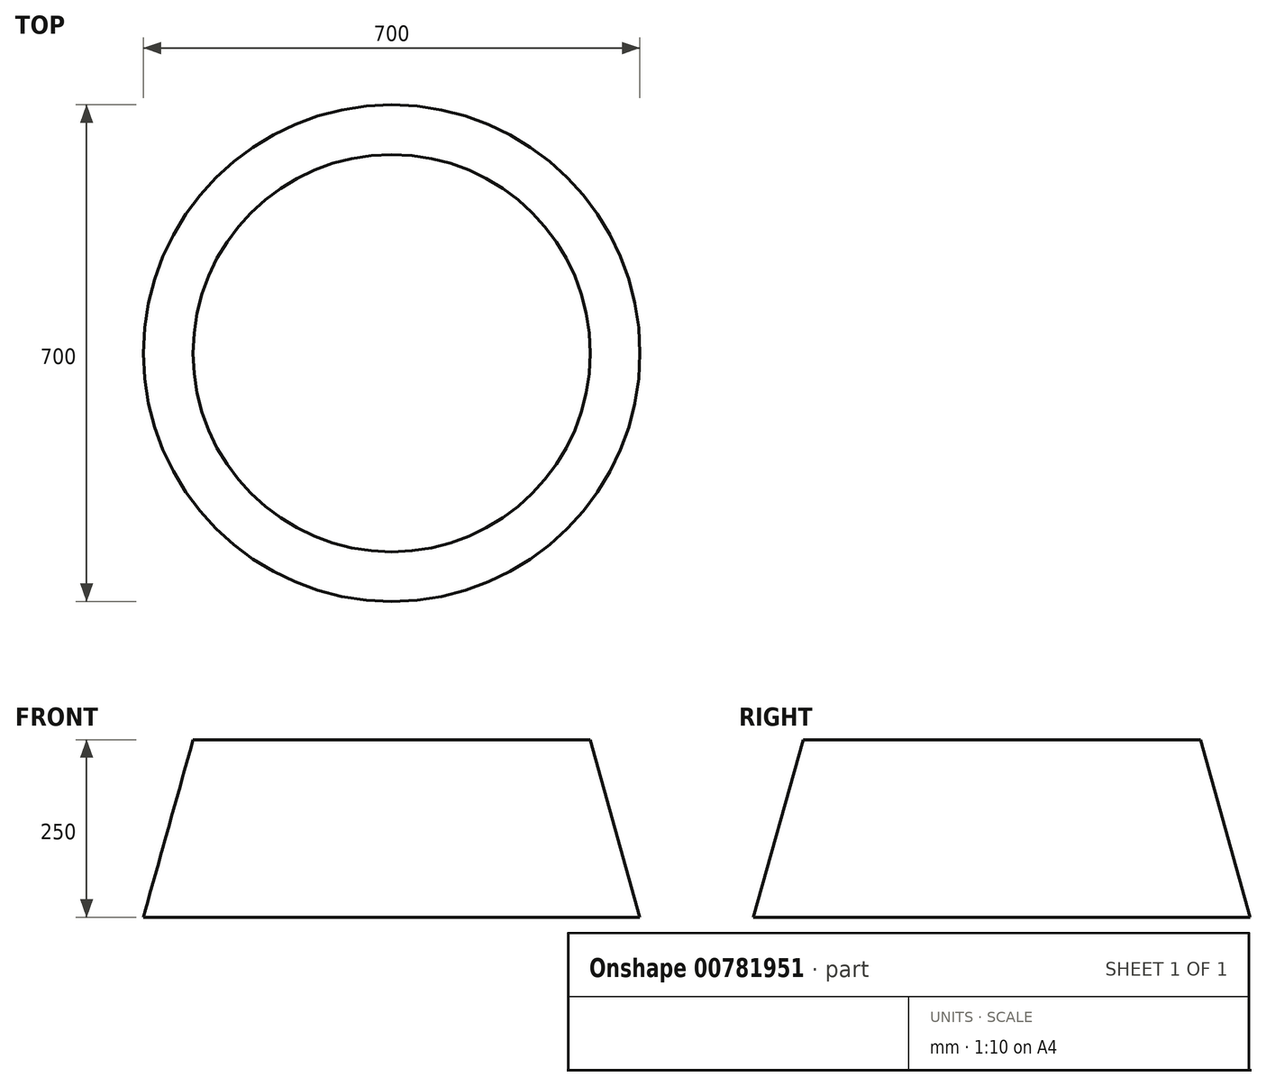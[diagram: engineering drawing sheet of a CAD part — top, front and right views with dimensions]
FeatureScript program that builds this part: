
annotation { "Feature Type Name" : "Feature", "Feature Type Description" : "" }
export const myFeature = defineFeature(function(context is Context, id is Id, definition is map)
    precondition{}
    {
        {
            var Q0;
            Q0=qCreatedBy(makeId("Front.planeOp"),FACE);
            var sketch = newSketch(context, id + "F0", { "sketchPlane" : qUnion([Q0])});
            skLineSegment(sketch, "E0", {"start": v(350, 0) * mm, "end": v(0, 0) * mm});
            skLineSegment(sketch, "E1", {"start": v(0, 0) * mm, "end": v(0, 250) * mm});
            skLineSegment(sketch, "E2", {"start": v(0, 250) * mm, "end": v(280, 250) * mm});
            skLineSegment(sketch, "E3", {"start": v(280, 250) * mm, "end": v(350, 0) * mm});
            skSolve(sketch);
        }
        {
            var Q0;
            Q0=makeQuery(id+"F0.imprint","IMPRINT",FACE,{"disambiguationData":[TD([[makeQuery(id+"F0.imprint","IMPRINT",EDGE,{"derivedFrom":sQuery(id+"F0.wireOp",EDGE,"E0")}),-1.0]])]});
            var Q1;
            Q1=sQuery(id+"F0.wireOp",EDGE,"E1");
            revolve(context, id + "F1", {"surfaceOperationType" : NewSurfaceOperationType.NEW, "entities" : qUnion([Q0]), "axis" : qUnion([Q1]), "revolveType" : RevolveType.FULL});
        }
    });
